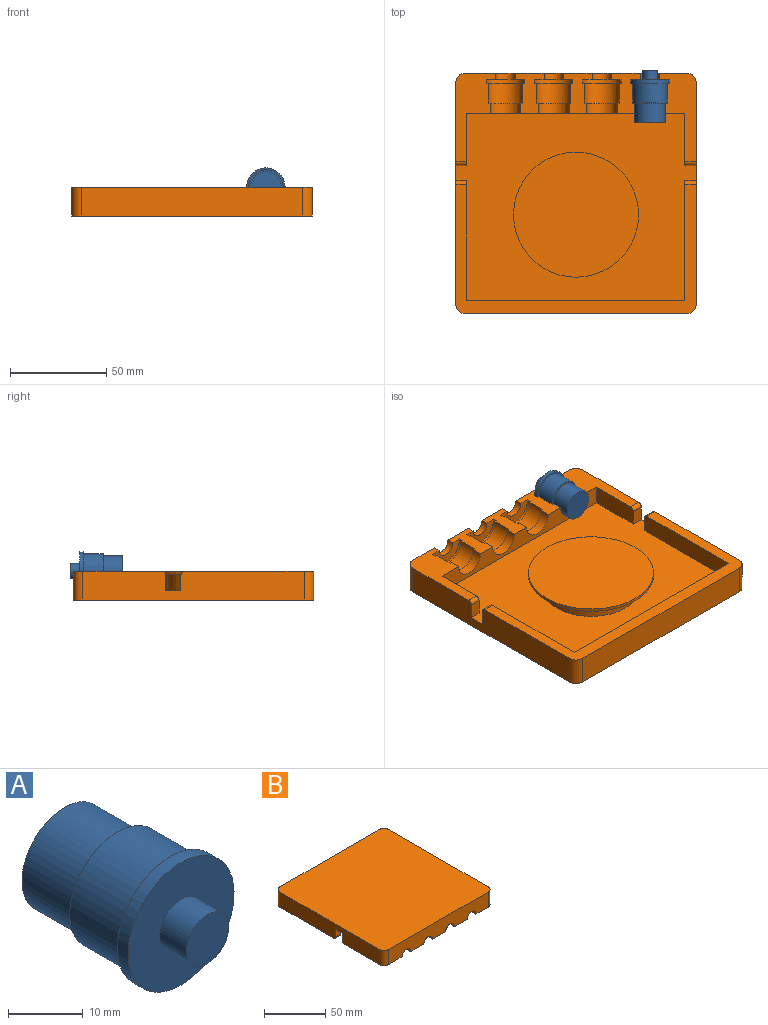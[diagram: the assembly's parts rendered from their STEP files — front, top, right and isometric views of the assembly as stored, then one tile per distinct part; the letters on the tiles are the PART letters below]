
ASSEMBLY  parts=2 mates=1
PART A: 9 faces, bbox 20x27x20 mm
  f0: cylinder r=9mm len=18mm, axis (0,-1,0), area 565.5mm2, adj f1,f4
  f1: plane 18x18mm, normal (0,1,0), area 53.4mm2, adj f0,f5
  f2: cylinder r=10mm len=20mm, axis (0,1,0), area 125.7mm2, adj f3,f4
  f3: plane 20x20mm, normal (0,-1,0), area 263.9mm2, adj f2,f7
  f4: plane 20x20mm, normal (0,1,0), area 59.7mm2, adj f0,f2
  f5: cylinder r=8mm len=16mm, axis (0,-1,0), area 502.7mm2, adj f1,f6
  f6: plane 16x16mm, normal (0,1,0), area 201.1mm2, adj f5
  f7: cylinder r=4mm len=8mm, axis (0,1,0), area 125.7mm2, adj f3,f8
  f8: plane 8x8mm, normal (0,-1,0), area 50.3mm2, adj f7
PART B: 62 faces, bbox 125x125x15 mm
  f0: plane 46.01x19.1mm, normal (0,0,-1), area 474.9mm2, adj f10,f12,f13,f14,f39,f40,f41,f42
  f1: plane 46.01x20.9mm, normal (0,0,-1), area 507.1mm2, adj f7,f12,f18,f19,f21,f22,f23,f24
  f2: plane 62.05x10mm, normal (1,0,0), area 619.7mm2, adj f11,f48,f49,f53,f55
  f3: plane 62.05x10mm, normal (-1,0,0), area 619.7mm2, adj f11,f48,f49,f50,f57
  f4: plane 20.8x15mm, normal (0,0,-1), area 180.2mm2, adj f7,f8,f12,f21,f22,f23,f24,f25
  f5: plane 20.8x15mm, normal (0,0,-1), area 180.2mm2, adj f8,f9,f12,f27,f28,f29,f30,f31
  f6: plane 20.8x15mm, normal (0,0,-1), area 180.2mm2, adj f9,f10,f12,f33,f34,f35,f36,f37
  f7: cylinder r=8mm len=16mm, axis (0,-1,0), area 133.3mm2, adj f1,f4,f25,f46
  f8: cylinder r=8mm len=16mm, axis (0,-1,0), area 133.3mm2, adj f4,f5,f31,f46
  f9: cylinder r=8mm len=16mm, axis (0,-1,0), area 133.3mm2, adj f5,f6,f37,f46
  f10: cylinder r=8mm len=16mm, axis (0,-1,0), area 133.3mm2, adj f0,f6,f43,f46
  f11: plane 125x67mm, normal (0,0,-1), area 1553.6mm2, adj f2,f3,f14,f15,f16,f17,f18,f48
  f12: plane 115x15mm, normal (0,-1,0), area 1567.9mm2, adj f0,f1,f4,f5,f6,f13,f19,f20
  f13: cylinder r=5mm len=15mm, axis (0,0,-1), area 117.8mm2, adj f0,f12,f14,f20
  f14: plane 115x15mm, normal (1,0,0), area 1643.3mm2, adj f0,f11,f13,f15,f20,f49,f50,f51
  f15: cylinder r=5mm len=15mm, axis (0,0,-1), area 117.8mm2, adj f11,f14,f16,f20
  f16: plane 115x15mm, normal (0,1,0), area 1725mm2, adj f11,f15,f17,f20
  f17: cylinder r=5mm len=15mm, axis (0,0,-1), area 117.8mm2, adj f11,f16,f18,f20
  f18: plane 115x15mm, normal (-1,0,0), area 1643.3mm2, adj f1,f11,f17,f19,f20,f49,f52,f53
  f19: cylinder r=5mm len=15mm, axis (0,0,-1), area 117.8mm2, adj f1,f12,f18,f20
  f20: plane 125x125mm, normal (0,0,1), area 15603.5mm2, adj f12,f13,f14,f15,f16,f17,f18,f19
  f21: cylinder r=10mm len=20mm, axis (0,1,0), area 62.8mm2, adj f1,f4,f22,f23
  f22: plane 20x10mm, normal (0,1,0), area 117.8mm2, adj f1,f4,f21,f26
  f23: plane 20x10mm, normal (0,-1,0), area 29.8mm2, adj f1,f4,f21,f24
  f24: cylinder r=9mm len=18mm, axis (0,-1,0), area 282.7mm2, adj f1,f4,f23,f25
  f25: plane 18x9mm, normal (0,-1,0), area 26.7mm2, adj f1,f4,f7,f24
  f26: cylinder r=5mm len=10mm, axis (0,1,0), area 55mm2, adj f1,f4,f12,f22
  f27: cylinder r=10mm len=20mm, axis (0,1,0), area 62.8mm2, adj f4,f5,f28,f29
  f28: plane 20x10mm, normal (0,1,0), area 117.8mm2, adj f4,f5,f27,f32
  f29: plane 20x10mm, normal (0,-1,0), area 29.8mm2, adj f4,f5,f27,f30
  f30: cylinder r=9mm len=18mm, axis (0,-1,0), area 282.7mm2, adj f4,f5,f29,f31
  f31: plane 18x9mm, normal (0,-1,0), area 26.7mm2, adj f4,f5,f8,f30
  f32: cylinder r=5mm len=10mm, axis (0,1,0), area 55mm2, adj f4,f5,f12,f28
  f33: cylinder r=10mm len=20mm, axis (0,1,0), area 62.8mm2, adj f5,f6,f34,f35
  f34: plane 20x10mm, normal (0,1,0), area 117.8mm2, adj f5,f6,f33,f38
  f35: plane 20x10mm, normal (0,-1,0), area 29.8mm2, adj f5,f6,f33,f36
  f36: cylinder r=9mm len=18mm, axis (0,-1,0), area 282.7mm2, adj f5,f6,f35,f37
  f37: plane 18x9mm, normal (0,-1,0), area 26.7mm2, adj f5,f6,f9,f36
  f38: cylinder r=5mm len=10mm, axis (0,1,0), area 55mm2, adj f5,f6,f12,f34
  f39: cylinder r=10mm len=20mm, axis (0,1,0), area 62.8mm2, adj f0,f6,f40,f41
  f40: plane 20x10mm, normal (0,1,0), area 117.8mm2, adj f0,f6,f39,f44
  f41: plane 20x10mm, normal (0,-1,0), area 29.8mm2, adj f0,f6,f39,f42
  f42: cylinder r=9mm len=18mm, axis (0,-1,0), area 282.7mm2, adj f0,f6,f41,f43
  f43: plane 18x9mm, normal (0,-1,0), area 26.7mm2, adj f0,f6,f10,f42
  f44: cylinder r=5mm len=10mm, axis (0,1,0), area 55mm2, adj f0,f6,f12,f40
  f45: plane 27.2x10mm, normal (1,0,0), area 271.2mm2, adj f1,f46,f49,f52,f54
  f46: plane 113.4x10mm, normal (0,1,0), area 731.8mm2, adj f0,f1,f4,f5,f6,f7,f8,f9
  f47: plane 27.2x10mm, normal (-1,0,0), area 271.2mm2, adj f0,f46,f49,f51,f56
  f48: plane 113.4x10mm, normal (0,-1,0), area 1134mm2, adj f2,f3,f11,f49
  f49: plane 125x97.26mm, normal (0,0,-1), area 9157.8mm2, adj f2,f3,f14,f18,f45,f46,f47,f48
  f50: plane 8x5.91mm, normal (0,-1,0), area 47.2mm2, adj f3,f14,f49,f57
  f51: plane 8x5.91mm, normal (0,1,0), area 47.2mm2, adj f14,f47,f49,f56
  f52: plane 8x5.7mm, normal (0,1,0), area 45.6mm2, adj f18,f45,f49,f54
  f53: plane 8x5.7mm, normal (0,-1,0), area 45.6mm2, adj f2,f18,f49,f55
  f54: cylinder r=2mm len=5.7mm, axis (-1,0,0), area 17.9mm2, adj f1,f18,f45,f52
  f55: cylinder r=2mm len=5.7mm, axis (1,0,0), area 17.9mm2, adj f2,f11,f18,f53
  f56: cylinder r=2mm len=5.91mm, axis (-1,0,0), area 18.6mm2, adj f0,f14,f47,f51
  f57: cylinder r=2mm len=5.91mm, axis (1,0,0), area 18.6mm2, adj f3,f11,f14,f50
  f58: cylinder r=25mm len=50mm, axis (0,0,-1), area 1335.2mm2, adj f49,f60
  f59: cylinder r=32.5mm len=65mm, axis (0,0,-1), area 306.3mm2, adj f60,f61
  f60: plane 65x65mm, normal (0,0,1), area 1354.8mm2, adj f58,f59
  f61: plane 65x65mm, normal (0,0,-1), area 3318.3mm2, adj f59
PLACE A rot(axis=(0,0,-1),180deg) t=(43.06,-67.06,12.22)mm
PLACE B rot(axis=(-1,0,0),180deg) t=(4.66,-124.06,12.22)mm
MATE cylindrical A.f2 <-> B.f44  axis (0,1,0) through (43.06,-65.06,12.22)mm
